# Revit family: EU_SINGLE_IDU_4WAY_CST_MINI_Ver.1.2
name_source: partatom
category: Mechanical Equipment
revit_build: Autodesk Revit 2016 (Build: 20150220_1215(x64)
units: mm (PartAtom-declared; Revit-internal decimal feet)

## family parameters
Always vertical = Yes
Cut with Voids When Loaded = No
Part Type = Normal
Room Calculation Point = No
Round Connector Dimension = Use Radius
Shared = No
Work Plane-Based = No

## types (23) — shared parameters
Manufacturer = SAMSUNG
Model = AC071RNNDKG/EU
Motor Output = 65 W
Refrigerant Type = R32
URL = www.samsung.com

## per-type parameters (varying)
| type | Net Weight | Panel Model | Panel Net Weight |
| 2.60 kW, 220-240V, SINGLE 4Way Cassette S (600*600)-A | 12.00 kg | PC4SUSMAN | 2.70 kg |
| 3.50 kW, 220-240V, SINGLE 4Way Cassette S (600*600)-A | 12.00 kg | PC4SUSMAN | 2.70 kg |
| 2.60 kW, 220-240V, SINGLE 4Way Cassette S (600*600)-B | 11.40 kg | PC4SUSMAN | 2.70 kg |
| 3.50 kW, 220-240V, SINGLE 4Way Cassette S (600*600)-B | 11.40 kg | PC4SUSMAN | 2.70 kg |
| 5.00 kW, 220-240V, SINGLE 4Way Cassette S (600*600) | 11.60 kg | PC4SUSMAN | 2.70 kg |
| 5.80 kW, 220-240V, SINGLE 4Way Cassette S (600*600) | 11.60 kg | PC4SUSMAN | 2.70 kg |
| 6.80 kW, 220-240V, SINGLE 4Way Cassette S (600*600) | 11.80 kg | PC4SUSMAN | 2.70 kg |
| 6.80 kW, 220-240V, SINGLE 4Way Cassette S (600*600, New panel) | 11.80 kg | PC4SUSMBN | 2.30 kg |
| 5.80 kW, 220-240V, SINGLE 4Way Cassette S (600*600, New panel) | 11.60 kg | PC4SUSMBN | 2.30 kg |
| 5.00 kW, 220-240V, SINGLE 4Way Cassette S (600*600, New panel) | 11.60 kg | PC4SUSMBN | 2.30 kg |
| 2.60 kW, 220-240V, SINGLE 4Way Cassette S (600*600, New panel)-A | 12.00 kg | PC4SUSMBN | 2.30 kg |
| 3.50 kW, 220-240V, SINGLE 4Way Cassette S (600*600, New panel)-A | 12.00 kg | PC4SUSMBN | 2.30 kg |
| 2.60 kW, 220-240V, SINGLE 4Way Cassette S (600*600, New panel)-B | 11.40 kg | PC4SUSMBN | 2.30 kg |
| 3.50 kW, 220-240V, SINGLE 4Way Cassette S (600*600, New panel)-B | 11.40 kg | PC4SUSMBN | 2.30 kg |
| 2.60 kW,  220-240V, 4WAY CASSETTE MINI, WIND FREE | 11.40 kg | PC4SUFMAN | 2.70 kg |
| 3.50 kW,  220-240V, 4WAY CASSETTE MINI, WIND FREE | 11.40 kg | PC4SUFMAN | 2.70 kg |
| 5.00 kW,  220-240V, 4WAY CASSETTE MINI, WIND FREE | 11.60 kg | PC4SUFMAN | 2.70 kg |
| 5.80 kW,  220-240V, 4WAY CASSETTE MINI, WIND FREE | 11.60 kg | PC4SUFMAN | 2.70 kg |
| 6.80 kW,  220-240V, 4WAY CASSETTE MINI, WIND FREE | 11.80 kg | PC4SUFMAN | 2.70 kg |
| 2.6kW, 220-240V, 4WAY CASSETTE Mini, R32 | 11.40 kg | PC4SUFMAN | 2.70 kg |
| 3.5kW, 220-240V, 4WAY CASSETTE Mini, R32 | 11.40 kg | PC4SUFMAN | 2.70 kg |
| 5.2kW, 220-240V, 4WAY CASSETTE Mini, R32 | 11.60 kg | PC4SUFMAN | 2.70 kg |
| 6.0kW, 220-240V, 4WAY CASSETTE Mini, R32 | 11.80 kg | PC4SUFMAN | 2.70 kg |

## geometry (parser evidence)
native form markers: Sweep x14
no freeform markers — native parametric forms only
